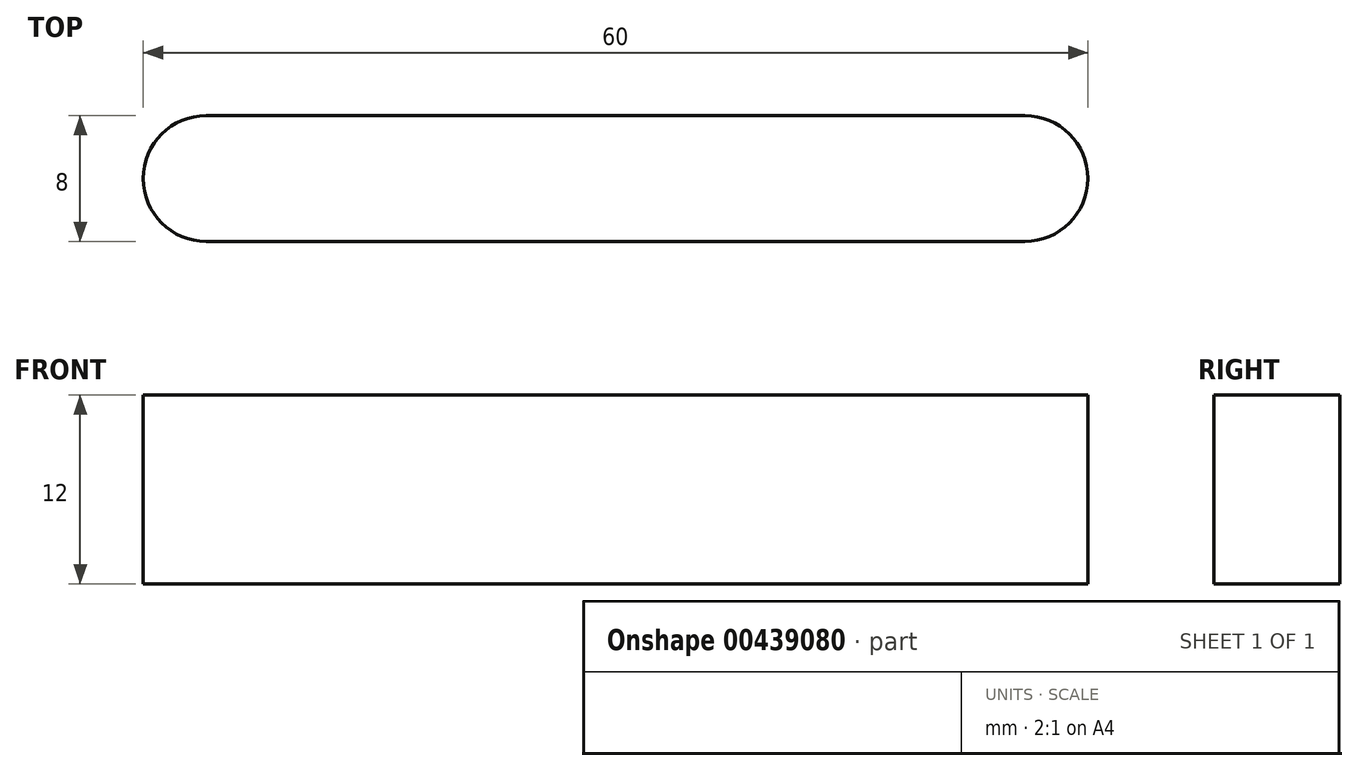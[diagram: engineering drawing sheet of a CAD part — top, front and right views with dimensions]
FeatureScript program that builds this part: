
annotation { "Feature Type Name" : "Feature", "Feature Type Description" : "" }
export const myFeature = defineFeature(function(context is Context, id is Id, definition is map)
    precondition{}
    {
        {
            var Q0;
            Q0=qCreatedBy(makeId("Top.planeOp"),FACE);
            var sketch = newSketch(context, id + "F0", { "sketchPlane" : qUnion([Q0])});
            skLineSegment(sketch, "E0.bottom", {"start": v(-9.7, 4.3) * mm, "end": v(42.3, 4.3) * mm});
            skLineSegment(sketch, "E0.top", {"start": v(-9.7, -3.7) * mm, "end": v(42.3, -3.7) * mm});
            skLineSegment(sketch, "E0.left", {"start": v(-9.7, 4.3) * mm, "end": v(-9.7, -3.7) * mm});
            skLineSegment(sketch, "E0.right", {"start": v(42.3, 4.3) * mm, "end": v(42.3, -3.7) * mm});
            skArc(sketch, "E1", {"start": v(-9.7, 4.3) * mm, "mid": v(-13.7, 0.3) * mm, "end": v(-9.7, -3.7) * mm});
            skArc(sketch, "E2", {"start": v(42.3, -3.7) * mm, "mid": v(46.3, 0.3) * mm, "end": v(42.3, 4.3) * mm});
            skSolve(sketch);
        }
        {
            var Q0;
            Q0 = qSketchRegion(id + "F0", true);
            extrude(context, id + "F1", {"entities" : qUnion([Q0]), "depth" : 12 * mm});
        }
    });
